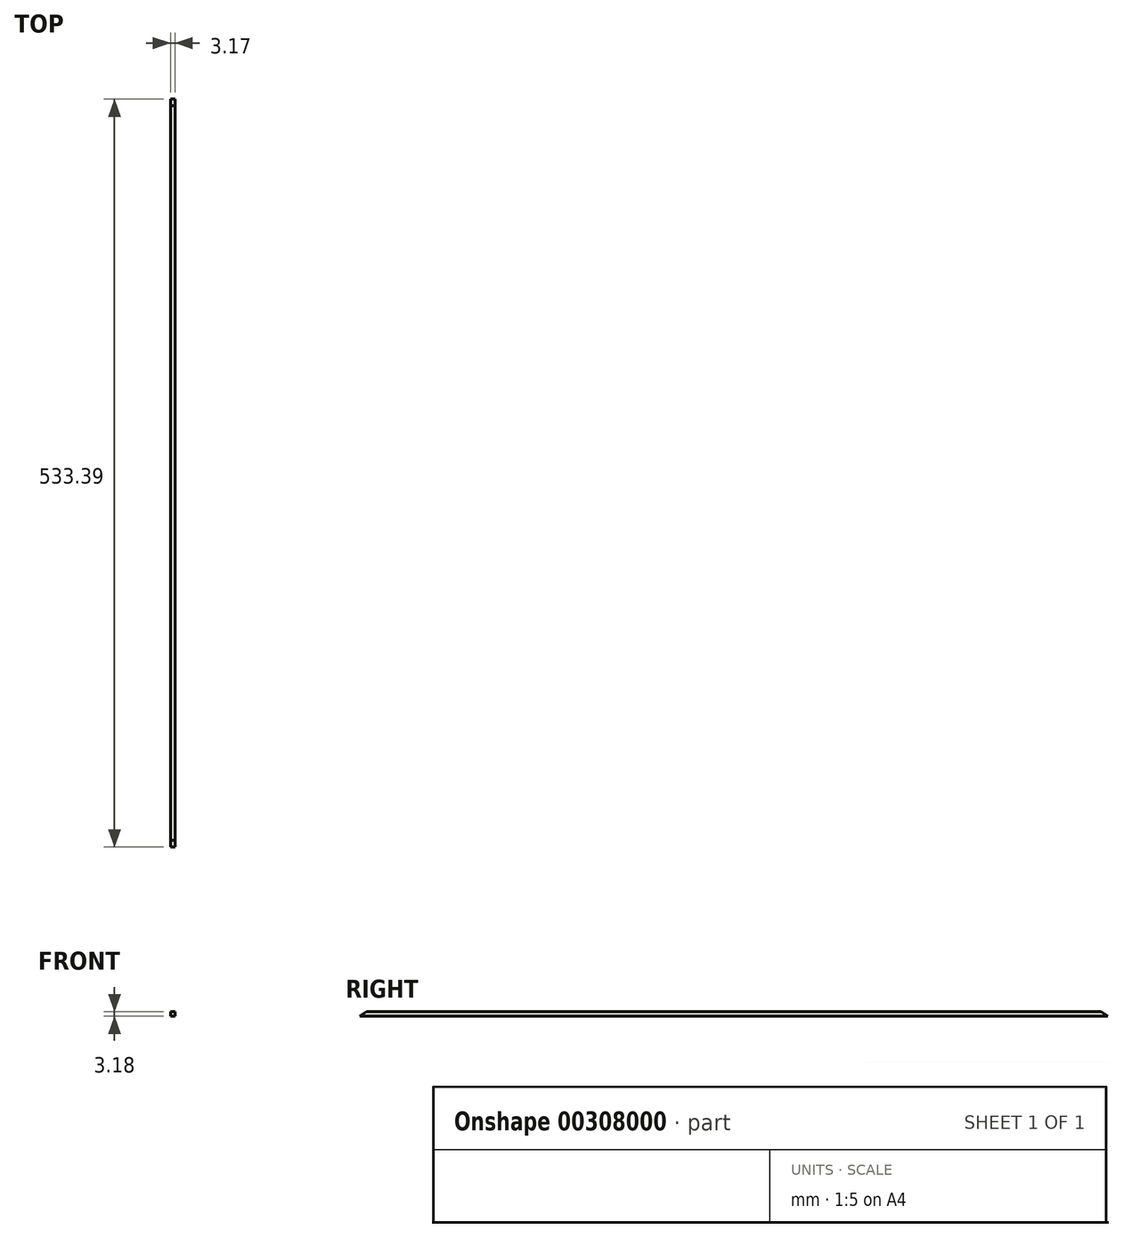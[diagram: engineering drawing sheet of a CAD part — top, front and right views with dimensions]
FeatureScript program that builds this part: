
annotation { "Feature Type Name" : "Feature", "Feature Type Description" : "" }
export const myFeature = defineFeature(function(context is Context, id is Id, definition is map)
    precondition{}
    {
        {
            var Q0;
            Q0=qCreatedBy(makeId("Right.planeOp"),FACE);
            var sketch = newSketch(context, id + "F0", { "sketchPlane" : qUnion([Q0])});
            skLineSegment(sketch, "E0", {"start": v(264.16, 0) * mm, "end": v(-269.23, 0) * mm});
            skLineSegment(sketch, "E1.1", {"start": v(259.34, 3.17) * mm, "end": v(-264.42, 3.17) * mm});
            skLineSegment(sketch, "E2", {"start": v(259.34, 3.17) * mm, "end": v(264.16, 0) * mm});
            skLineSegment(sketch, "E3", {"start": v(-264.42, 3.17) * mm, "end": v(-269.23, 0) * mm});
            skSolve(sketch);
        }
        {
            var Q0;
            Q0=makeQuery(id+"F0.imprint","IMPRINT",FACE,{"disambiguationData":[TD([[makeQuery(id+"F0.imprint","IMPRINT",EDGE,{"derivedFrom":sQuery(id+"F0.wireOp",EDGE,"E0")}),-1.0]])]});
            var Q1;
            {var subQ0=sQuery(id+"F0.wireOp",EDGE,"lpvmD4Qc-t4Sp-Q4cq-c35C-fVnn1vbR4N0d");Q1=makeQuery(id+"F0.imprint","IMPRINT",FACE,{"disambiguationData":[TD([[makeQuery(id+"F0.imprint","IMPRINT",EDGE,{"derivedFrom":subQ0}),-1.0]])]});}
            var Q2;
            {var subQ0=sQuery(id+"F0.wireOp",EDGE,"Zd5pBiKY-3EBp-Sm5Y-wHDk-2GRI8JiMUKWk");Q2=makeQuery(id+"F0.imprint","IMPRINT",FACE,{"disambiguationData":[TD([[makeQuery(id+"F0.imprint","IMPRINT",EDGE,{"derivedFrom":subQ0}),1.0]])]});}
            extrude(context, id + "F1", {"entities" : qUnion([Q0, Q1, Q2]), "depth" : 3.17 * mm});
        }
    });
